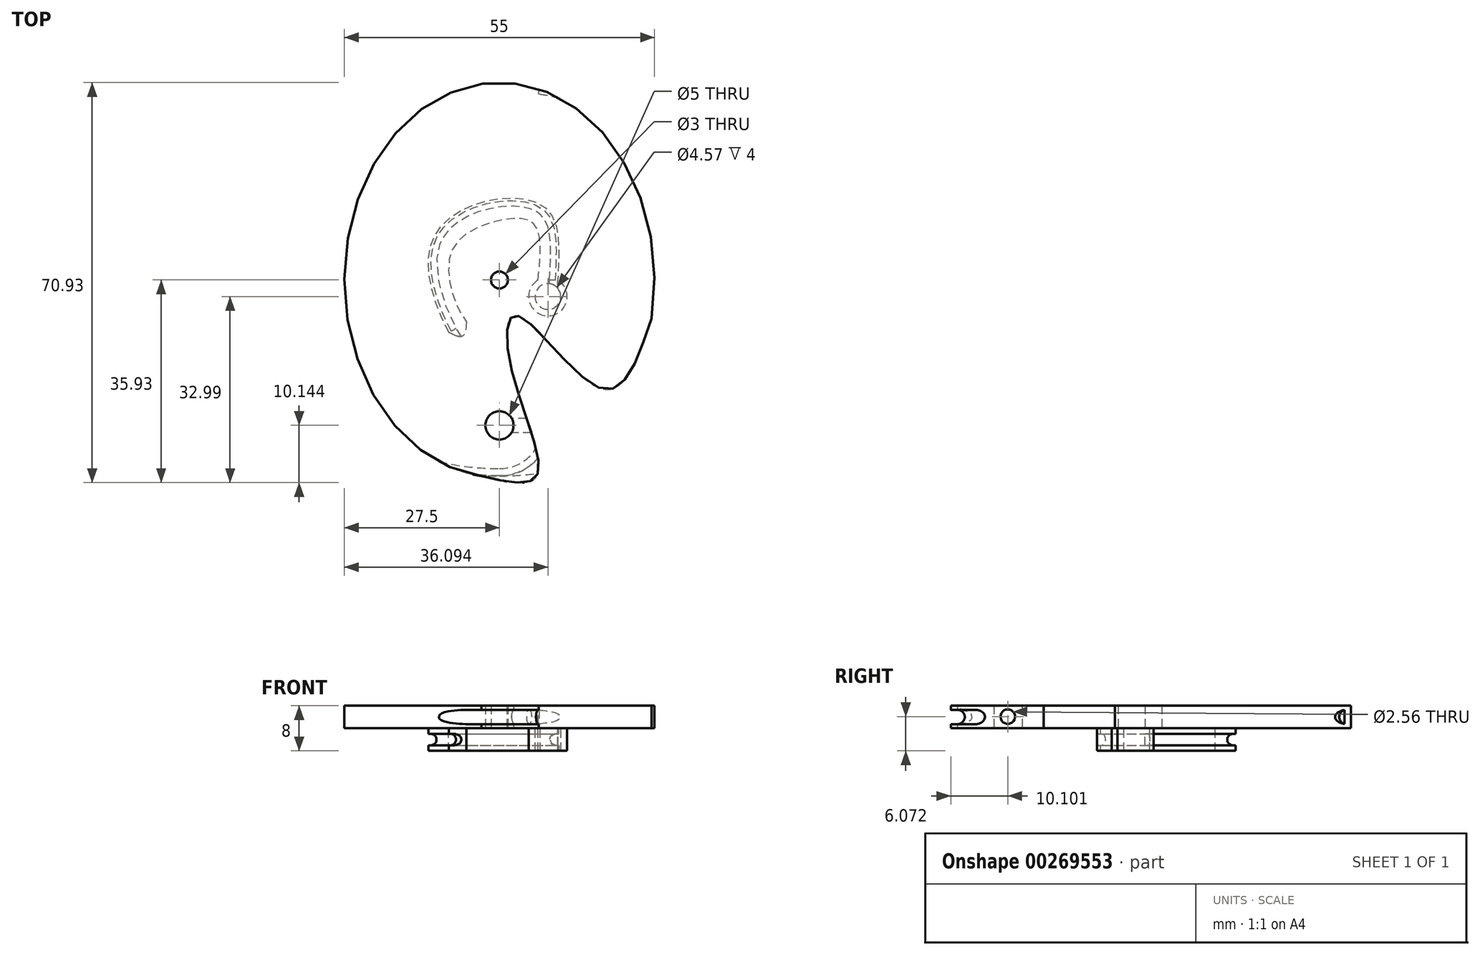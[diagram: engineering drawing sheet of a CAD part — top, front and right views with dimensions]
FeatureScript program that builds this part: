
annotation { "Feature Type Name" : "Feature", "Feature Type Description" : "" }
export const myFeature = defineFeature(function(context is Context, id is Id, definition is map)
    precondition{}
    {
        {
            var Q0;
            Q0=qCreatedBy(makeId("Top.planeOp"),FACE);
            var sketch = newSketch(context, id + "F8", { "sketchPlane" : qUnion([Q0])});
            skCircle(sketch, "E0", {"center": v(0, -25.79) * mm, "radius": 2.5 * mm});
            skEllipticalArc(sketch, "E1.trimOffspring", {});
            skPoint(sketch, "E2.3.internal.orphan", {"position": v(9.5, 0) * mm});
            skPoint(sketch, "E3.0.internal.orphan", {"position": v(18.35, -6.83) * mm});
            skPoint(sketch, "E3.1.internal.orphan", {"position": v(23.13, -20.33) * mm});
            skPoint(sketch, "E3.2.internal.orphan", {"position": v(26.97, -6.83) * mm});
            skPoint(sketch, "E4.orphan", {"position": v(23.13, -14.08) * mm});
            skFitSpline(sketch, "E5", {"points": [v(-3.19, -34.76) * mm, v(6.6, -34.76) * mm, v(2.01, -15.29) * mm, v(3.15, -6.29) * mm, v(18.34, -19.35) * mm, v(26.97, -6.83) * mm], "startDerivative": vector(78.13, -18.35) * mm, "endDerivative": vector(32.68, 98.5) * mm});
            skCircle(sketch, "E6", {"center": v(0, 0) * mm, "radius": 1.5 * mm});
            const initialGuessFD7VVaR5RRnER9FFF_0  = {"E1.trimOffspring": [0, 0, 0, -1, 0.035, 0.0275, 1.3742742962770849, 6.167059260959714]};
            skSetInitialGuess(sketch, initialGuessFD7VVaR5RRnER9FFF_0);
            skSolve(sketch);
        }
        {
            var Q0;
            Q0=makeQuery(id+"F8.imprint","IMPRINT",FACE,{"disambiguationData":[TD([[makeQuery(id+"F8.imprint","IMPRINT",EDGE,{"derivedFrom":sQuery(id+"F8.wireOp",EDGE,"E0")}),-1.0]])]});
            extrude(context, id + "F9", {"entities" : qUnion([Q0]), "depth" : 4 * mm});
        }
        {
            var Q0;
            Q0=qCreatedBy(makeId("Right.planeOp"),FACE);
            var sketch = newSketch(context, id + "F10", { "sketchPlane" : qUnion([Q0])});
            skCircle(sketch, "E7", {"center": v(-25.83, 2.07) * mm, "radius": 1.28 * mm});
            skSolve(sketch);
        }
        {
            var Q0;
            Q0 = qSketchRegion(id + "F10", true);
            extrude(context, id + "F0", {"entities" : qUnion([Q0]), "operationType" : NewBodyOperationType.REMOVE, "depth" : 25 * mm});
        }
        {
            var Q0;
            Q0=qCreatedBy(makeId("Right.planeOp"),FACE);
            var sketch = newSketch(context, id + "F11", { "sketchPlane" : qUnion([Q0])});
            skArc(sketch, "E8", {"start": v(-34.7, 0.74) * mm, "mid": v(-33.46, 2.04) * mm, "end": v(-34.76, 3.29) * mm});
            skLineSegment(sketch, "E9", {"start": v(-34.76, 3.29) * mm, "end": v(-34.7, 0.74) * mm});
            skLineSegment(sketch, "E10", {"start": v(-34.7, 0.74) * mm, "end": v(-38.27, 0.74) * mm});
            skLineSegment(sketch, "E11", {"start": v(-38.27, 0.74) * mm, "end": v(-38.27, 3.3) * mm});
            skLineSegment(sketch, "E12", {"start": v(-38.27, 3.3) * mm, "end": v(-34.76, 3.29) * mm});
            skSolve(sketch);
        }
        {
            var Q0;
            Q0 = qSketchRegion(id + "F11", true);
            var Q1;
            Q1=makeQuery(id+"F9.opExtrude","CAP_EDGE",EDGE,{"disambiguationData":[OSD([sQuery(id+"F8.wireOp",EDGE,"E1.trimOffspring")])],"isStart":false});
            sweep(context, id + "F12", {"operationType" : NewBodyOperationType.REMOVE, "profiles" : qUnion([Q0]), "path" : qUnion([Q1])});
        }
        {
            var Q0;
            Q0 = qSketchRegion(id + "F11", true);
            var Q1;
            Q1=makeQuery(id+"F9.opExtrude","CAP_EDGE",EDGE,{"disambiguationData":[OSD([sQuery(id+"F8.wireOp",EDGE,"E0")])],"isStart":false});
            revolve(context, id + "F13", {"operationType" : NewBodyOperationType.REMOVE, "entities" : qUnion([Q0]), "axis" : qUnion([Q1]), "revolveType" : RevolveType.ONE_DIRECTION, "angle" : 90 * degree});
        }
        {
            var Q0;
            Q0=makeQuery(id+"F9.opExtrude","CAP_FACE",FACE,{"disambiguationData":[OSD([sQuery(id+"F8.wireOp",EDGE,"E0"),sQuery(id+"F8.wireOp",EDGE,"E1.trimOffspring"),sQuery(id+"F8.wireOp",EDGE,"E5"),sQuery(id+"F8.wireOp",EDGE,"E6")])],"isStart":true});
            var sketch = newSketch(context, id + "F1", { "sketchPlane" : qUnion([Q0])});
            skArc(sketch, "E13", {"start": v(10.34, 0) * mm, "mid": v(8.6, 6.36) * mm, "end": v(6.85, 0) * mm});
            skFitSpline(sketch, "E14", {"points": [v(10.34, 0) * mm, v(8.63, -12.34) * mm, v(-2.38, -13.99) * mm, v(-11.98, -6.8) * mm, v(-8.95, 9.34) * mm], "startDerivative": vector(3.16, -59.25) * mm, "endDerivative": vector(31.46, 59.29) * mm});
            skFitSpline(sketch, "E15", {"points": [v(6.85, 0) * mm, v(6.23, -9.79) * mm, v(0, -10.52) * mm, v(-8.63, -4.67) * mm, v(-5.86, 7.37) * mm, v(-2.38, 9.34) * mm], "startDerivative": vector(5.88, -55.7) * mm, "endDerivative": vector(26.85, 5.5) * mm});
            skFitSpline(sketch, "E16", {"points": [v(-5.86, 7.37) * mm, v(-6.48, 9.93) * mm, v(-8.95, 9.34) * mm], "startDerivative": vector(-0.28, 6.63) * mm, "endDerivative": vector(-5.9, -2.73) * mm});
            skCircle(sketch, "E17", {"center": v(8.6, 2.94) * mm, "radius": 2.29 * mm});
            skSolve(sketch);
        }
        {
            var Q0;
            Q0=makeQuery(id+"F1.imprint","IMPRINT",FACE,{"disambiguationData":[TD([[makeQuery(id+"F1.imprint","IMPRINT",EDGE,{"derivedFrom":sQuery(id+"F1.wireOp",EDGE,"E13")}),1.0]])]});
            extrude(context, id + "F2", {"entities" : qUnion([Q0]), "operationType" : NewBodyOperationType.ADD, "depth" : 4 * mm});
        }
        {
            var Q0;
            Q0=makeQuery(id+"F2.opExtrude","CAP_FACE",FACE,{"disambiguationData":[OSD([sQuery(id+"F1.wireOp",EDGE,"E13"),sQuery(id+"F1.wireOp",EDGE,"E14"),sQuery(id+"F1.wireOp",EDGE,"E15"),sQuery(id+"F1.wireOp",EDGE,"E16"),sQuery(id+"F1.wireOp",EDGE,"E17")])],"isStart":false});
            var sketch = newSketch(context, id + "F14", { "sketchPlane" : qUnion([Q0])});
            skLineSegment(sketch, "E18", {"start": v(-8.95, 9.34) * mm, "end": v(-5.86, 7.37) * mm, "construction": true});
            skSolve(sketch);
        }
        {
            var Q0;
            Q0=sQuery(id+"F14.wireOp",EDGE,"E18");
            var Q1;
            Q1=qCreatedBy(makeId("Front.planeOp"),FACE);
            cPlane(context, id + "F3", {"entities" : qUnion([Q0, Q1]), "cplaneType" : CPlaneType.LINE_ANGLE, "offset" : 25 * mm, "angle" : 0 * degree, "width" : 150 * mm, "height" : 150 * mm});
        }
        {
            var Q0;
            Q0=qCreatedBy(id+"F3.planeOp",FACE);
            var sketch = newSketch(context, id + "F4", { "sketchPlane" : qUnion([Q0])});
            skLineSegment(sketch, "E19.0", {"start": v(12.57, -4) * mm, "end": v(12.57, 0) * mm});
            skLineSegment(sketch, "E20.bottom", {"start": v(12.57, -3) * mm, "end": v(12.1, -3) * mm});
            skLineSegment(sketch, "E20.top", {"start": v(12.57, -1) * mm, "end": v(12.1, -1) * mm});
            skLineSegment(sketch, "E20.left", {"start": v(12.57, -3) * mm, "end": v(12.57, -1) * mm});
            skLineSegment(sketch, "E20.right", {"start": v(12.1, -3) * mm, "end": v(12.1, -1) * mm});
            skArc(sketch, "E21", {"start": v(12.1, -1) * mm, "mid": v(11.1, -2) * mm, "end": v(12.1, -3) * mm});
            skSolve(sketch);
        }
        {
            var Q0;
            Q0 = qSketchRegion(id + "F4", true);
            var Q1;
            Q1=makeQuery(id+"F2.opExtrude","CAP_EDGE",EDGE,{"disambiguationData":[OSD([sQuery(id+"F1.wireOp",EDGE,"E14")])],"isStart":false});
            sweep(context, id + "F5", {"operationType" : NewBodyOperationType.REMOVE, "profiles" : qUnion([Q0]), "path" : qUnion([Q1])});
        }
        {
            var Q0;
            Q0 = qSketchRegion(id + "F4", true);
            extrude(context, id + "F6", {"entities" : qUnion([Q0]), "operationType" : NewBodyOperationType.REMOVE, "oppositeDirection" : true, "depth" : 25 * mm});
        }
        {
            var Q0;
            Q0=makeQuery(id+"F5.boolean.opBoolean","COPY",FACE,{"derivedFrom":makeQuery(id+"F5.opSweep","CAP_FACE",FACE,{"disambiguationData":[OSD([sQuery(id+"F1.wireOp",EDGE,"E13"),sQuery(id+"F1.wireOp",EDGE,"E14"),sQuery(id+"F4.wireOp",EDGE,"E20.bottom"),sQuery(id+"F4.wireOp",EDGE,"E20.top"),sQuery(id+"F4.wireOp",EDGE,"E20.left"),sQuery(id+"F4.wireOp",EDGE,"E21")])],"isStart":false})});
            var sketch = newSketch(context, id + "F7", { "sketchPlane" : qUnion([Q0])});
            skArc(sketch, "E22.0", {"start": v(-9.87, -1) * mm, "mid": v(-8.87, -2) * mm, "end": v(-9.87, -3) * mm});
            skLineSegment(sketch, "E23.0", {"start": v(-9.87, -3) * mm, "end": v(-10.34, -3) * mm});
            skLineSegment(sketch, "E24.0", {"start": v(-10.34, -3) * mm, "end": v(-10.34, -1) * mm});
            skLineSegment(sketch, "E25.0", {"start": v(-10.34, -1) * mm, "end": v(-9.87, -1) * mm});
            skSolve(sketch);
        }
        {
            var Q0;
            Q0=makeQuery(id+"F7.imprint","IMPRINT",FACE,{"disambiguationData":[TD([[makeQuery(id+"F7.imprint","IMPRINT",EDGE,{"derivedFrom":sQuery(id+"F7.wireOp",EDGE,"E22.0")}),-1.0]])]});
            extrude(context, id + "F15", {"entities" : qUnion([Q0]), "operationType" : NewBodyOperationType.REMOVE, "endBound" : BoundingType.UP_TO_NEXT, "oppositeDirection" : true, "depth" : 25 * mm});
        }
    });
